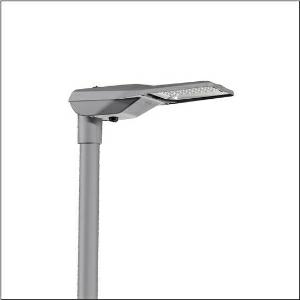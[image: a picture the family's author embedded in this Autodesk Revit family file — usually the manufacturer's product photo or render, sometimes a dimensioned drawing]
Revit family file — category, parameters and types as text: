
# Revit family: streetlight_sl_21_mini___p0_8a_5xe2u33t08hb_848e
name_source: partatom
category: Lighting Fixtures
units: mm (PartAtom-declared; Revit-internal decimal feet)

## family parameters
Cut with Voids When Loaded = No
Host = Face
Light Source = No
Part Type = Normal
Room Calculation Point = No
Round Connector Dimension = Use Diameter
Shared = No

## types (1)
- --- (1 x LED, 9120 lm, 66 W, 3000K)
    Apparent Load = 66 VA
    CIE Flux Codes = 33 69 96 100 100
    Color Rendering = 70
    Color Temperature = 3000K
    Default Elevation = 1800 mm
    Description = Streetlight SL 21 mini, mast luminaire, primary light control with lens, of PMMA, primary optical cover: cover, of toughened safety glass, transparent, light distribution: P0.8a, light emission: direct distribution, primary light characteristic: asymmetric, installation type: post-top, side-entry, LED, High Power LED, rated luminous flux: 9.120lm, luminous efficacy: 138lm/W, light colour: 730, colour temperature: 3000K, control gear: D4i, control: pre-setting: logarithmic dimming characteristic, flexible luminous flux parameterisation, time-dependent luminous flux control, constant luminous flux control, overheat protection, mains connection: 220..240V, AC, 50/60Hz, start of lifetime: 66W, end of service life: 69W, reduction: 30W, luminaire housing, of diecast aluminium, powder-coated, Siteco® metallic grey (DB 702S), corrosivity category C5 mid according to DIN EN ISO 12944, multi-level sealing system, sealing non-destructively replaceable, inclination adjustable: 0°, 5°, 10°, 15°, please order mast flange separately, length: 628mm, width: 235mm, height: 110mm, mast flange for spigot size: 42mm (side-entry): 5XC10008XM4, 60/48mm (side-entry/post-top): 5XC10108XM2, 76/60mm (side-entry/post-top): 5XC10108XM1, mounting height: 4..8m, Smart Interface below and above, protection rating (complete): IP66, insulation class (complete): insulation class II (safety insulation), certification: CE, ENEC, ENEC+, VDE, impact resistance: IK10, permissible operating ambient temperature for outdoor applications: -40..+50°C, standard-compliant lighting for roads and squares, packaging unit: 1 piece

Light Distribution: P0.8a
    Height = 110 mm
    Lamp = 1 x LED
    Lamp Light Flux = 9120 lm
    Lamp Power = 66 W
    Lamp count = 1
    Length = 625 mm
    Luminous efficacy = 138 lm/W
    Manufacturer = Siteco
    ModVariant = No
    Model = 5XE2U33T08HB
    Number of Poles = 1
    OnlyDefault = Yes
    Power Factor = 1
    Product Name = Streetlight SL 21 mini | P0.8a
    Product group = mast luminaire | pylon top
    ProductGroupID = 6100
    Protection Class = Protection class II
    Protection Degree = IP 66
    RLX_Detail_Level = 1
    RLX_Emergency_Light_Flux = 0 lm
    RLX_Emergency_Type = 0
    RLX_Emergency_Type_DB = No
    RlxData = <blob elided: 26005 chars, md5=081bf90d>
    Socket = socket
    Standby Power = 0 W
    System Light Flux = 9120 lm
    System Power = 66 W
    Type Comments = factory setting: luminous flux: 100 % | dim-lin: 254 | 670 mA
    Type Image = l_1003514.jpg
    URL = http://relux.com
    VarID = @adj_072478
    Voltage = 0 V
    Weight = 0.00 kg
    Width = 234 mm

## geometry (parser evidence)
native form markers: Blend x4, Sweep x8
no freeform markers — native parametric forms only
